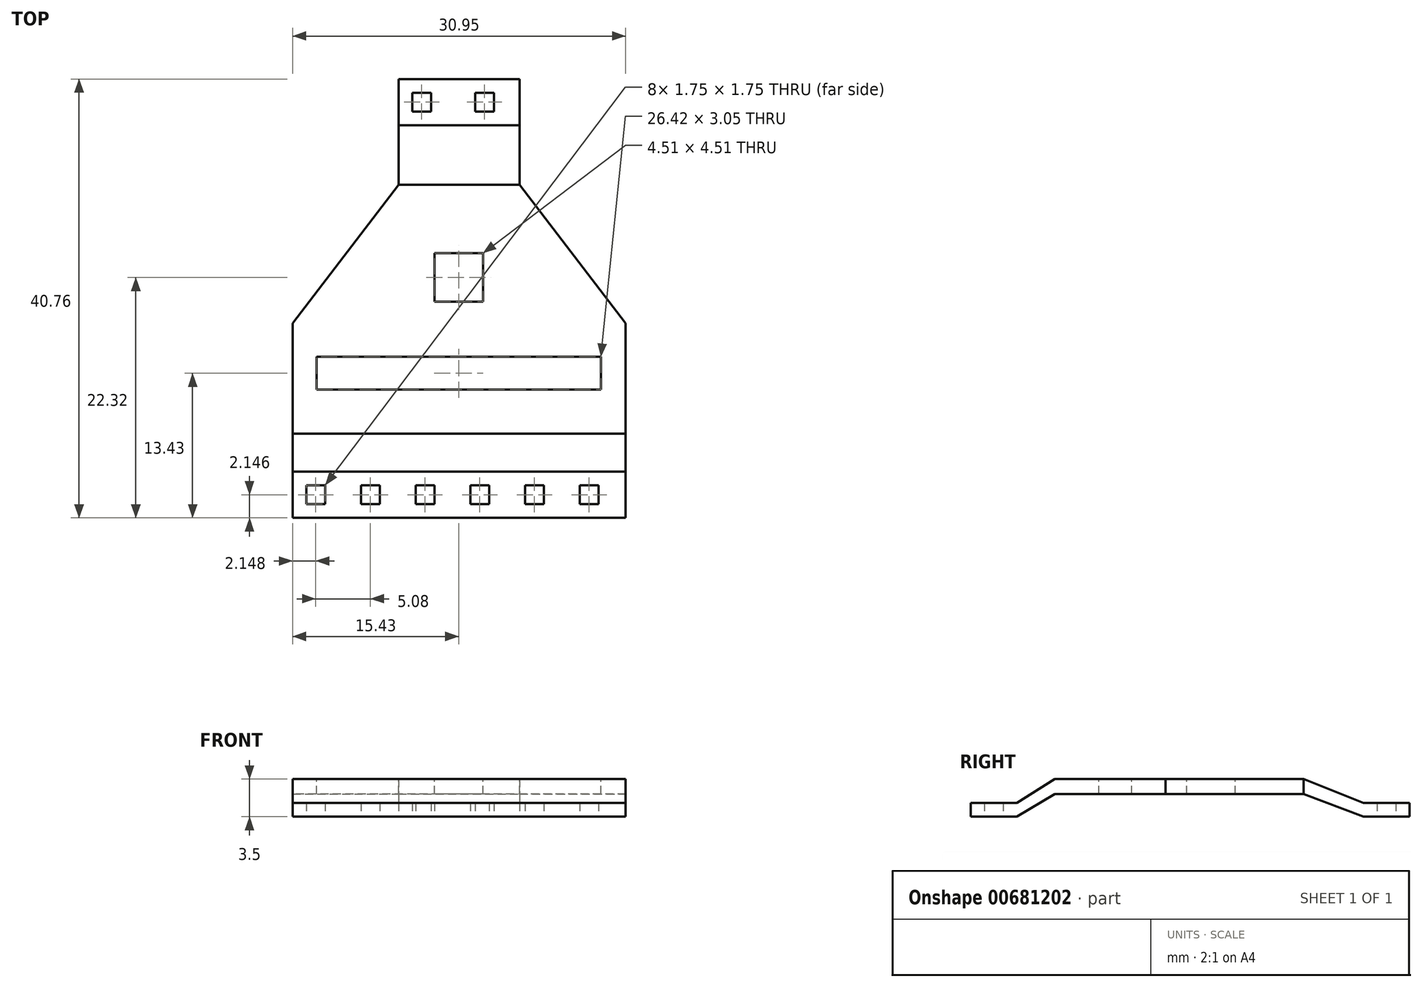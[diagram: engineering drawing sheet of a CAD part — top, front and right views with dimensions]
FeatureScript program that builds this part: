
annotation { "Feature Type Name" : "Feature", "Feature Type Description" : "" }
export const myFeature = defineFeature(function(context is Context, id is Id, definition is map)
    precondition{}
    {
        {
            var Q0;
            Q0=makeQuery(id+"FVILoqW2jpY53VQ.importOp","IMPORT",FACE,{"importTag":102.0});
            cPoint(context, id + "F0", {"pointType" : PointType.MESH_POINT, "mesh" : qUnion([Q0]), "x" : -12.7 * mm, "y" : -7.62 * mm, "z" : 0.27 * mm});
        }
        {
            var Q0;
            Q0=makeQuery(id+"FVILoqW2jpY53VQ.importOp","IMPORT",FACE,{"importTag":102.0});
            cPoint(context, id + "F1", {"pointType" : PointType.MESH_POINT, "mesh" : qUnion([Q0]), "x" : 12.7 * mm, "y" : -7.62 * mm, "z" : 0.27 * mm});
        }
        {
            var Q0;
            Q0=makeQuery(id+"FVILoqW2jpY53VQ.importOp","IMPORT",FACE,{"importTag":102.0});
            cPoint(context, id + "F2", {"pointType" : PointType.MESH_POINT, "mesh" : qUnion([Q0]), "x" : 12.7 * mm, "y" : 7.62 * mm, "z" : 0.27 * mm});
        }
        {
            var Q0;
            Q0=qCreatedBy(id+"F0",VERTEX);
            var Q1;
            Q1=qCreatedBy(id+"F1",VERTEX);
            var Q2;
            Q2=qCreatedBy(id+"F2",VERTEX);
            cPlane(context, id + "F3", {"entities" : qUnion([Q0, Q1, Q2]), "cplaneType" : CPlaneType.THREE_POINT, "offset" : 25.4 * mm, "width" : 152.4 * mm, "height" : 152.4 * mm});
        }
        {
            var Q0;
            Q0=qCreatedBy(id+"F3.planeOp",FACE);
            var sketch = newSketch(context, id + "F4", { "sketchPlane" : qUnion([Q0])});
            skPoint(sketch, "E0.0", {"position": v(-12.7, 7.62) * mm});
            skPoint(sketch, "E1.0", {"position": v(12.7, 7.62) * mm});
            skLineSegment(sketch, "E2.bottom", {"start": v(-12.7, 7.62) * mm, "end": v(12.7, 7.62) * mm});
            skLineSegment(sketch, "E2.top", {"start": v(-12.7, 5.08) * mm, "end": v(12.7, 5.08) * mm});
            skLineSegment(sketch, "E2.left", {"start": v(-12.7, 7.62) * mm, "end": v(-12.7, 5.08) * mm});
            skLineSegment(sketch, "E2.right", {"start": v(12.7, 7.62) * mm, "end": v(12.7, 5.08) * mm});
            skSolve(sketch);
        }
        {
            var Q0;
            Q0=qSketchRegion(id+"F4",true);
            extrude(context, id + "F5", {"entities" : qUnion([Q0]), "oppositeDirection" : true, "depth" : 5.08 * mm, "offsetDistance" : 25.4 * mm});
        }
        {
            var Q0;
            Q0=qCreatedBy(id+"F3.planeOp",FACE);
            cPlane(context, id + "F6", {"entities" : qUnion([Q0]), "cplaneType" : CPlaneType.OFFSET, "offset" : 1.9 * mm, "oppositeDirection" : true, "width" : 152.4 * mm, "height" : 152.4 * mm});
        }
        {
            var Q0;
            Q0=qCreatedBy(id+"F6.planeOp",FACE);
            var sketch = newSketch(context, id + "F7", { "sketchPlane" : qUnion([Q0])});
            skLineSegment(sketch, "E3.bottom", {"start": v(15.52, 11.97) * mm, "end": v(-15.43, 11.97) * mm});
            skLineSegment(sketch, "E3.top", {"start": v(15.52, 1.7) * mm, "end": v(-15.43, 1.7) * mm});
            skLineSegment(sketch, "E3.left", {"start": v(15.52, 11.97) * mm, "end": v(15.52, 1.7) * mm});
            skLineSegment(sketch, "E3.right", {"start": v(-15.43, 11.97) * mm, "end": v(-15.43, 1.7) * mm});
            skLineSegment(sketch, "E4", {"start": v(-5.58, -11.15) * mm, "end": v(5.67, -11.15) * mm});
            skLineSegment(sketch, "E5", {"start": v(-15.43, 1.7) * mm, "end": v(-5.58, -11.15) * mm});
            skLineSegment(sketch, "E6", {"start": v(5.67, -11.15) * mm, "end": v(15.52, 1.7) * mm});
            skLineSegment(sketch, "E7.0", {"start": v(-12.7, 5.08) * mm, "end": v(12.7, 5.08) * mm});
            skLineSegment(sketch, "E8.0", {"start": v(-12.7, 7.62) * mm, "end": v(12.7, 7.62) * mm});
            skLineSegment(sketch, "E9.0.0", {"start": v(-12.7, 5.08) * mm, "end": v(-12.7, 7.62) * mm});
            skLineSegment(sketch, "E9.0.2", {"start": v(12.7, 7.62) * mm, "end": v(12.7, 5.08) * mm});
            skLineSegment(sketch, "E9.0.3", {"start": v(12.7, 5.08) * mm, "end": v(-12.7, 5.08) * mm});
            skLineSegment(sketch, "E10.bottom", {"start": v(13.2, 7.87) * mm, "end": v(-13.2, 7.87) * mm});
            skLineSegment(sketch, "E10.top", {"start": v(13.2, 4.83) * mm, "end": v(-13.2, 4.83) * mm});
            skLineSegment(sketch, "E10.left", {"start": v(13.2, 7.87) * mm, "end": v(13.2, 4.83) * mm});
            skLineSegment(sketch, "E10.right", {"start": v(-13.2, 7.87) * mm, "end": v(-13.2, 4.83) * mm});
            skPoint(sketch, "E11.0", {"position": v(-2, -4.54) * mm});
            skPoint(sketch, "E11.1", {"position": v(2, -4.54) * mm});
            skPoint(sketch, "E11.2", {"position": v(2, -0.54) * mm});
            skPoint(sketch, "E12.0", {"position": v(-2, -0.54) * mm});
            skLineSegment(sketch, "E13.bottom", {"start": v(2, -0.54) * mm, "end": v(-2, -0.54) * mm});
            skLineSegment(sketch, "E13.top", {"start": v(2, -4.54) * mm, "end": v(-2, -4.54) * mm});
            skLineSegment(sketch, "E13.left", {"start": v(2, -0.54) * mm, "end": v(2, -4.54) * mm});
            skLineSegment(sketch, "E13.right", {"start": v(-2, -0.54) * mm, "end": v(-2, -4.54) * mm});
            skLineSegment(sketch, "E14.bottom", {"start": v(2.25, -0.29) * mm, "end": v(-2.25, -0.29) * mm});
            skLineSegment(sketch, "E14.top", {"start": v(2.25, -4.8) * mm, "end": v(-2.25, -4.8) * mm});
            skLineSegment(sketch, "E14.left", {"start": v(2.25, -0.29) * mm, "end": v(2.25, -4.8) * mm});
            skLineSegment(sketch, "E14.right", {"start": v(-2.25, -0.29) * mm, "end": v(-2.25, -4.8) * mm});
            skPoint(sketch, "E15", {"position": v(0.05, -11.15) * mm});
            skPoint(sketch, "E16", {"position": v(0.05, 1.7) * mm});
            skLineSegment(sketch, "E17", {"start": v(0.05, 1.7) * mm, "end": v(0.05, -11.15) * mm});
            skSolve(sketch);
        }
        {
            var Q0;
            Q0=makeQuery(id+"F7.imprint","IMPRINT",FACE,{"disambiguationData":[TD([[makeQuery(id+"F7.imprint","IMPRINT",EDGE,{"derivedFrom":sQuery(id+"F7.wireOp",EDGE,"E3.bottom")}),1.0]])]});
            var Q1;
            {var subQ4=sQuery(id+"F7.wireOp",EDGE,"E6");Q1=makeQuery(id+"F7.imprint","IMPRINT",FACE,{"disambiguationData":[TD([[makeQuery(id+"F7.imprint","IMPRINT",EDGE,{"derivedFrom":subQ4}),1.0]])]});}
            var Q2;
            {var subQ4=sQuery(id+"F7.wireOp",EDGE,"E5");Q2=makeQuery(id+"F7.imprint","IMPRINT",FACE,{"disambiguationData":[TD([[makeQuery(id+"F7.imprint","IMPRINT",EDGE,{"derivedFrom":subQ4}),1.0]])]});}
            extrude(context, id + "F8", {"entities" : qUnion([Q0, Q1, Q2]), "depth" : 1.4 * mm, "offsetDistance" : 25.4 * mm});
        }
        {
            var Q0;
            Q0=makeQuery(id+"FVILoqW2jpY53VQ.importOp","IMPORT",FACE,{"importTag":102.0});
            cPoint(context, id + "F9", {"pointType" : PointType.MESH_POINT, "mesh" : qUnion([Q0]), "x" : 8.84 * mm, "y" : 4.32 * mm, "z" : -1.33 * mm});
        }
        {
            var Q0;
            Q0=makeQuery(id+"FVILoqW2jpY53VQ.importOp","IMPORT",FACE,{"importTag":102.0});
            cPoint(context, id + "F10", {"pointType" : PointType.MESH_POINT, "mesh" : qUnion([Q0]), "x" : 1.78 * mm, "y" : -6.35 * mm, "z" : -1.33 * mm});
        }
        {
            var Q0;
            Q0=makeQuery(id+"FVILoqW2jpY53VQ.importOp","IMPORT",FACE,{"importTag":102.0});
            cPoint(context, id + "F11", {"pointType" : PointType.MESH_POINT, "mesh" : qUnion([Q0]), "x" : -9.4 * mm, "y" : 3.76 * mm, "z" : -1.33 * mm});
        }
        {
            var Q0;
            Q0=qCreatedBy(id+"F9",VERTEX);
            var Q1;
            Q1=qCreatedBy(id+"F10",VERTEX);
            var Q2;
            Q2=qCreatedBy(id+"F11",VERTEX);
            cPlane(context, id + "F12", {"entities" : qUnion([Q0, Q1, Q2]), "cplaneType" : CPlaneType.THREE_POINT, "offset" : 25.4 * mm, "width" : 152.4 * mm, "height" : 152.4 * mm});
        }
        {
            var Q0;
            Q0=qCreatedBy(id+"F12.planeOp",FACE);
            var sketch = newSketch(context, id + "F13", { "sketchPlane" : qUnion([Q0])});
            skPoint(sketch, "E18.0", {"position": v(15.52, -11.97) * mm});
            skPoint(sketch, "E19.0", {"position": v(-15.43, -11.97) * mm});
            skPoint(sketch, "E20.0", {"position": v(5.67, 11.15) * mm});
            skPoint(sketch, "E21.0", {"position": v(-5.58, 11.15) * mm});
            skLineSegment(sketch, "E22.bottom", {"start": v(-15.43, -15.49) * mm, "end": v(15.52, -15.49) * mm});
            skLineSegment(sketch, "E22.top", {"start": v(-15.43, -19.78) * mm, "end": v(15.52, -19.78) * mm});
            skLineSegment(sketch, "E22.left", {"start": v(-15.43, -15.49) * mm, "end": v(-15.43, -19.78) * mm});
            skLineSegment(sketch, "E22.right", {"start": v(15.52, -15.49) * mm, "end": v(15.52, -19.78) * mm});
            skLineSegment(sketch, "E23", {"start": v(-15.43, -11.97) * mm, "end": v(-15.43, -15.49) * mm});
            skLineSegment(sketch, "E24", {"start": v(15.52, -11.97) * mm, "end": v(15.52, -15.49) * mm});
            skLineSegment(sketch, "E25.bottom", {"start": v(-5.58, 20.98) * mm, "end": v(5.67, 20.98) * mm});
            skLineSegment(sketch, "E25.top", {"start": v(-5.58, 16.7) * mm, "end": v(5.67, 16.7) * mm});
            skLineSegment(sketch, "E25.left", {"start": v(-5.58, 16.7) * mm, "end": v(-5.58, 20.98) * mm});
            skLineSegment(sketch, "E25.right", {"start": v(5.67, 16.7) * mm, "end": v(5.67, 20.98) * mm});
            skLineSegment(sketch, "E26", {"start": v(-5.58, 20.98) * mm, "end": v(-5.58, 11.15) * mm});
            skLineSegment(sketch, "E27", {"start": v(5.67, 20.98) * mm, "end": v(5.67, 11.15) * mm});
            skLineSegment(sketch, "E28.bottom", {"start": v(-14.16, -16.76) * mm, "end": v(-12.4, -16.76) * mm});
            skLineSegment(sketch, "E28.top", {"start": v(-14.16, -18.5) * mm, "end": v(-12.4, -18.5) * mm});
            skLineSegment(sketch, "E28.left", {"start": v(-14.16, -16.76) * mm, "end": v(-14.16, -18.5) * mm});
            skLineSegment(sketch, "E28.right", {"start": v(-12.4, -16.76) * mm, "end": v(-12.4, -18.5) * mm});
            skLineSegment(sketch, "E29.1.0.0", {"start": v(-9.08, -16.76) * mm, "end": v(-9.08, -18.5) * mm});
            skLineSegment(sketch, "E29.1.0.1", {"start": v(-9.08, -18.5) * mm, "end": v(-7.33, -18.5) * mm});
            skLineSegment(sketch, "E29.1.0.2", {"start": v(-7.33, -16.76) * mm, "end": v(-7.33, -18.5) * mm});
            skLineSegment(sketch, "E29.1.0.3", {"start": v(-9.08, -16.76) * mm, "end": v(-7.33, -16.76) * mm});
            skLineSegment(sketch, "E29.2.0.0", {"start": v(-4, -16.76) * mm, "end": v(-4, -18.5) * mm});
            skLineSegment(sketch, "E29.2.0.1", {"start": v(-4, -18.5) * mm, "end": v(-2.25, -18.5) * mm});
            skLineSegment(sketch, "E29.2.0.2", {"start": v(-2.25, -16.76) * mm, "end": v(-2.25, -18.5) * mm});
            skLineSegment(sketch, "E29.2.0.3", {"start": v(-4, -16.76) * mm, "end": v(-2.25, -16.76) * mm});
            skLineSegment(sketch, "E29.3.0.0", {"start": v(1.08, -16.76) * mm, "end": v(1.08, -18.5) * mm});
            skLineSegment(sketch, "E29.3.0.1", {"start": v(1.08, -18.5) * mm, "end": v(2.83, -18.5) * mm});
            skLineSegment(sketch, "E29.3.0.2", {"start": v(2.83, -16.76) * mm, "end": v(2.83, -18.5) * mm});
            skLineSegment(sketch, "E29.3.0.3", {"start": v(1.08, -16.76) * mm, "end": v(2.83, -16.76) * mm});
            skLineSegment(sketch, "E29.4.0.0", {"start": v(6.16, -16.76) * mm, "end": v(6.16, -18.5) * mm});
            skLineSegment(sketch, "E29.4.0.1", {"start": v(6.16, -18.5) * mm, "end": v(7.91, -18.5) * mm});
            skLineSegment(sketch, "E29.4.0.2", {"start": v(7.91, -16.76) * mm, "end": v(7.91, -18.5) * mm});
            skLineSegment(sketch, "E29.4.0.3", {"start": v(6.16, -16.76) * mm, "end": v(7.91, -16.76) * mm});
            skLineSegment(sketch, "E29.5.0.0", {"start": v(11.24, -16.76) * mm, "end": v(11.24, -18.5) * mm});
            skLineSegment(sketch, "E29.5.0.1", {"start": v(11.24, -18.5) * mm, "end": v(13, -18.5) * mm});
            skLineSegment(sketch, "E29.5.0.2", {"start": v(13, -16.76) * mm, "end": v(13, -18.5) * mm});
            skLineSegment(sketch, "E29.5.0.3", {"start": v(11.24, -16.76) * mm, "end": v(13, -16.76) * mm});
            skLineSegment(sketch, "E29.direction1", {"start": v(-14.16, -18.5) * mm, "end": v(-9.08, -18.5) * mm, "construction": true});
            skLineSegment(sketch, "E30.bottom", {"start": v(-4.31, 19.71) * mm, "end": v(-2.56, 19.71) * mm});
            skLineSegment(sketch, "E30.top", {"start": v(-4.31, 17.96) * mm, "end": v(-2.56, 17.96) * mm});
            skLineSegment(sketch, "E30.left", {"start": v(-4.31, 19.71) * mm, "end": v(-4.31, 17.96) * mm});
            skLineSegment(sketch, "E30.right", {"start": v(-2.56, 19.71) * mm, "end": v(-2.56, 17.96) * mm});
            skLineSegment(sketch, "E31.1.0.0", {"start": v(1.53, 19.71) * mm, "end": v(1.53, 17.96) * mm});
            skLineSegment(sketch, "E31.1.0.1", {"start": v(1.53, 17.96) * mm, "end": v(3.28, 17.96) * mm});
            skLineSegment(sketch, "E31.1.0.2", {"start": v(3.28, 19.71) * mm, "end": v(3.28, 17.96) * mm});
            skLineSegment(sketch, "E31.1.0.3", {"start": v(1.53, 19.71) * mm, "end": v(3.28, 19.71) * mm});
            skLineSegment(sketch, "E31.direction1", {"start": v(-4.31, 17.96) * mm, "end": v(1.53, 17.96) * mm, "construction": true});
            skSolve(sketch);
        }
        {
            var Q0;
            Q0=makeQuery(id+"F13.imprint","IMPRINT",FACE,{"disambiguationData":[TD([[makeQuery(id+"F13.imprint","IMPRINT",EDGE,{"derivedFrom":sQuery(id+"F13.wireOp",EDGE,"E22.bottom")}),-1.0]])]});
            var Q1;
            {var subQ0=sQuery(id+"F13.wireOp",EDGE,"E25.bottom");Q1=makeQuery(id+"F13.imprint","IMPRINT",FACE,{"disambiguationData":[TD([[makeQuery(id+"F13.imprint","IMPRINT",EDGE,{"derivedFrom":subQ0}),-1.0]])]});}
            extrude(context, id + "F14", {"entities" : qUnion([Q0, Q1]), "depth" : 1.27 * mm, "offsetDistance" : 25.4 * mm});
        }
        {
            var Q0;
            Q0=makeQuery(id+"F14.opExtrude","SWEPT_FACE",FACE,{"disambiguationData":[OSD([sQuery(id+"F13.wireOp",EDGE,"E22.bottom")])]});
            var Q1;
            Q1=makeQuery(id+"F8.opExtrude","SWEPT_FACE",FACE,{"disambiguationData":[OSD([sQuery(id+"F7.wireOp",EDGE,"E3.bottom")])]});
            loft(context, id + "F15", {"operationType" : NewBodyOperationType.ADD, "sheetProfilesArray" : [{ "sheetProfileEntities" : qUnion([Q0]) }, { "sheetProfileEntities" : qUnion([Q1]) }]});
        }
        {
            var Q0;
            Q0=makeQuery(id+"F8.opExtrude","SWEPT_FACE",FACE,{"disambiguationData":[OSD([sQuery(id+"F7.wireOp",EDGE,"E4")])]});
            var Q1;
            Q1=makeQuery(id+"F14.opExtrude","SWEPT_FACE",FACE,{"disambiguationData":[OSD([sQuery(id+"F13.wireOp",EDGE,"E25.top")])]});
            loft(context, id + "F16", {"operationType" : NewBodyOperationType.ADD, "sheetProfilesArray" : [{ "sheetProfileEntities" : qUnion([Q0]) }, { "sheetProfileEntities" : qUnion([Q1]) }]});
        }
        {
            var Q0;
            Q0=makeQuery(id+"F5.opExtrude","SWEPT_BODY",BODY,{"disambiguationData":[OSD([sQuery(id+"F4.wireOp",EDGE,"E2.bottom"),sQuery(id+"F4.wireOp",EDGE,"E2.top"),sQuery(id+"F4.wireOp",EDGE,"E2.left"),sQuery(id+"F4.wireOp",EDGE,"E2.right")])]});
            deleteBodies(context, id + "F17", {"entities" : qUnion([Q0])});
        }
    });
